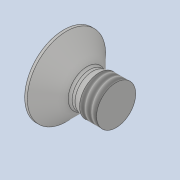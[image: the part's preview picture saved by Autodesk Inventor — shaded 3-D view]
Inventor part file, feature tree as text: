
AUTODESK INVENTOR PART (.ipt)
format: ipt  version: 2022 (Build 260153000, 153)  size: 152,576 bytes
history: native  units: mm
features: other x14, sketch x2, revolve x1, thread x1, extrude x1
ambient origin geometry x8: Origin, YZ Plane, XZ Plane, XY Plane, X Axis, Y Axis, Z Axis, Center Point
bodies: Solid1 (feature_tree)
feature tree (19):
  revolve  "Revolution1"  [1 undecoded]
  thread  "Thread1"  [1 undecoded]
  extrude  "Extrusion1"  [1 undecoded]
  other  "bolt_XY"
  other  "bolt_YZ"
  other  "bolt_ZX"
  other  "bolt_X"
  other  "bolt_Y"
  other  "bolt_Z"
  other  "bolt_Center"
  other  "nut_XY"
  other  "nut_YZ"
  other  "nut_ZX"
  other  "nut_X"
  other  "nut_Y"
  other  "nut_Z"
  other  "nut_Center"
  sketch  "Sketch_1"  dims[d0=360.0deg d1=2.6mm d2=0.0mm d3=1.7mm d4=0.0mm]
  sketch  "Sketch_2"  dims[d5=0.0mm d6=0.0mm]
note: 3 required parameter values undecoded (feature->parameter linkage not recoverable at this tier; creation-order binding heuristic only, values carry confidence <= 0.55)